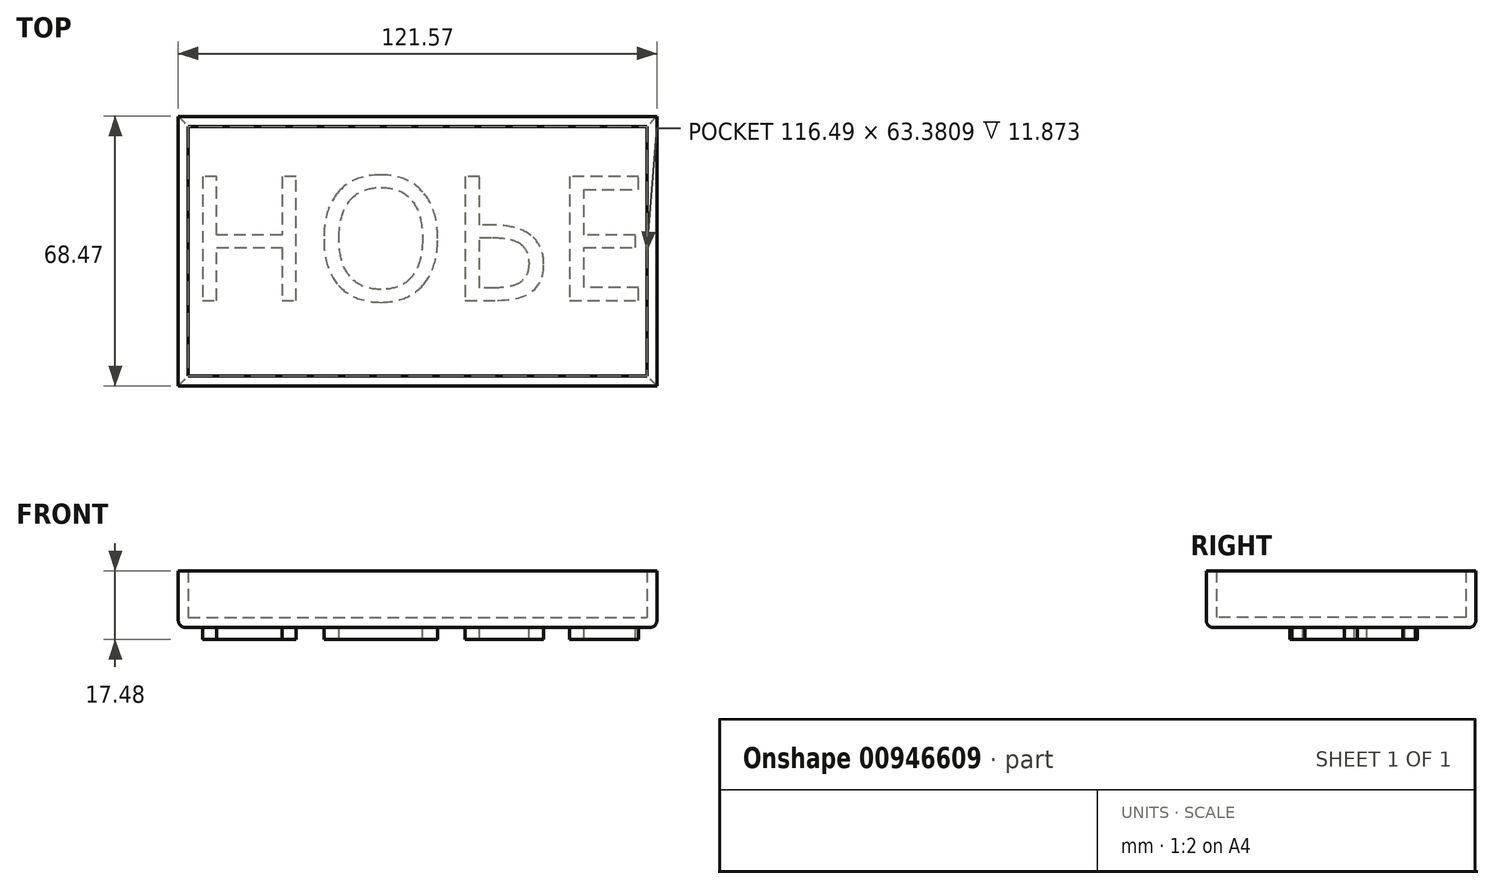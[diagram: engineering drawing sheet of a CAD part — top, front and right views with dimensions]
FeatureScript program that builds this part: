
annotation { "Feature Type Name" : "Feature", "Feature Type Description" : "" }
export const myFeature = defineFeature(function(context is Context, id is Id, definition is map)
    precondition{}
    {
        {
            var Q0;
            Q0=qCreatedBy(makeId("Top.planeOp"),FACE);
            var sketch = newSketch(context, id + "F0", { "sketchPlane" : qUnion([Q0])});
            skLineSegment(sketch, "E0.bottom", {"start": v(-53.73, 47.72) * mm, "end": v(67.84, 47.72) * mm});
            skLineSegment(sketch, "E0.top", {"start": v(-53.73, -20.75) * mm, "end": v(67.84, -20.75) * mm});
            skLineSegment(sketch, "E0.left", {"start": v(-53.73, 47.72) * mm, "end": v(-53.73, -20.75) * mm});
            skLineSegment(sketch, "E0.right", {"start": v(67.84, 47.72) * mm, "end": v(67.84, -20.75) * mm});
            skSolve(sketch);
        }
        {
            var Q0;
            Q0=makeQuery(id+"F0.imprint","IMPRINT",FACE,{"disambiguationData":[TD([[makeQuery(id+"F0.imprint","IMPRINT",EDGE,{"derivedFrom":sQuery(id+"F0.wireOp",EDGE,"E0.bottom")}),-1.0]])]});
            extrude(context, id + "F1", {"entities" : qUnion([Q0]), "depth" : 14.4 * mm, "offsetDistance" : 25.4 * mm});
        }
        {
            var Q0;
            Q0=makeQuery(id+"F1.opExtrude","CAP_FACE",FACE,{"disambiguationData":[OSD([sQuery(id+"F0.wireOp",EDGE,"E0.bottom"),sQuery(id+"F0.wireOp",EDGE,"E0.top"),sQuery(id+"F0.wireOp",EDGE,"E0.left"),sQuery(id+"F0.wireOp",EDGE,"E0.right")])],"isStart":false});
            shell(context, id + "F2", {"entities" : qUnion([Q0]), "thickness" : 2.54 * mm});
        }
        {
            var Q0;
            Q0=makeQuery(id+"F1.opExtrude","CAP_FACE",FACE,{"disambiguationData":[OSD([sQuery(id+"F0.wireOp",EDGE,"E0.bottom"),sQuery(id+"F0.wireOp",EDGE,"E0.top"),sQuery(id+"F0.wireOp",EDGE,"E0.left"),sQuery(id+"F0.wireOp",EDGE,"E0.right")])],"isStart":true});
            fillet(context, id + "F3", {"entities" : qUnion([Q0]), "radius" : 1.78 * mm, "tangentPropagation" : true, "allowEdgeOverflow" : false});
        }
        {
            var Q0;
            Q0=makeQuery(id+"F1.opExtrude","CAP_FACE",FACE,{"disambiguationData":[OSD([sQuery(id+"F0.wireOp",EDGE,"E0.bottom"),sQuery(id+"F0.wireOp",EDGE,"E0.top"),sQuery(id+"F0.wireOp",EDGE,"E0.left"),sQuery(id+"F0.wireOp",EDGE,"E0.right")])],"isStart":true});
            var sketch = newSketch(context, id + "F4", { "sketchPlane" : qUnion([Q0])});
            skText(sketch, "E1", { "text": "HOPE", "fontName": "OpenSans-Regular.ttf"});
            const initialGuessF4  = {"E1": [-0.05195, -0.03241, 1, 0, 0.03171]};
            skSetInitialGuess(sketch, initialGuessF4);
            skSolve(sketch);
        }
        {
            var Q0;
            Q0 = qSketchRegion(id + "F4", true);
            extrude(context, id + "F5", {"entities" : qUnion([Q0]), "operationType" : NewBodyOperationType.ADD, "depth" : 3.07 * mm, "offsetDistance" : 25.4 * mm});
        }
    });
